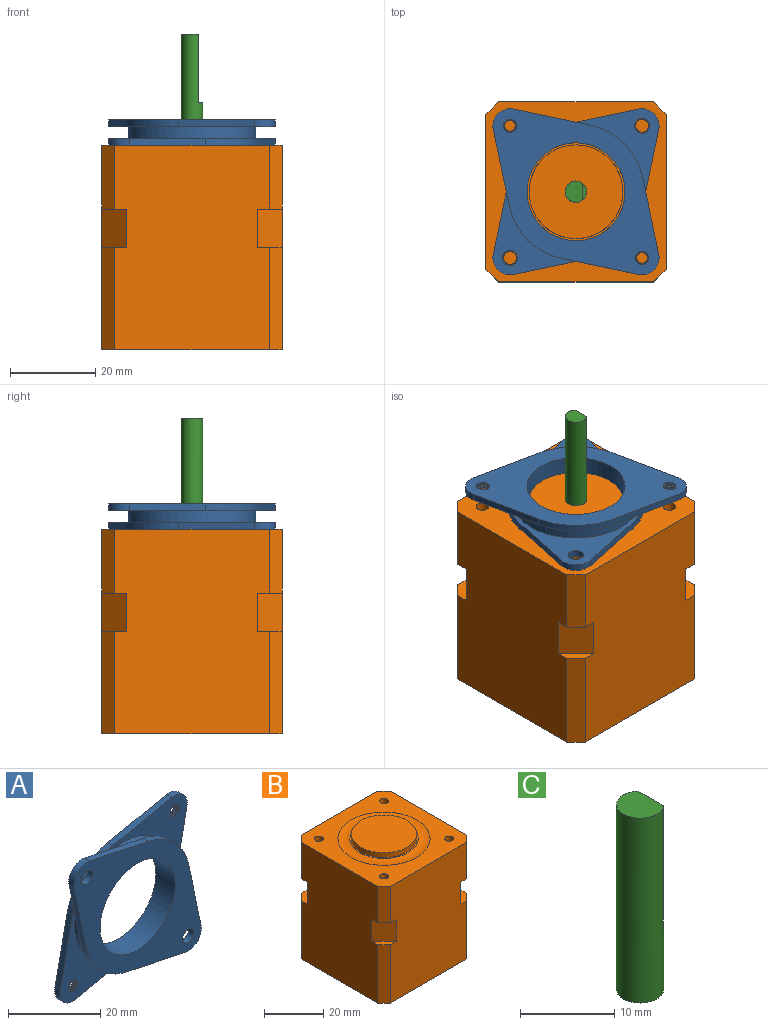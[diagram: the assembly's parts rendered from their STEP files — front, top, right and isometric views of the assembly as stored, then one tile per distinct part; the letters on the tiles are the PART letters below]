
ASSEMBLY  parts=3 mates=2
PART A: 32 faces, bbox 39.1x6.2x39.1 mm
  f0: cylinder r=1.75mm len=3.5mm, axis (0,1,0), area 17.6mm2, adj f10,f11
  f1: cylinder r=1.75mm len=3.5mm, axis (0,1,0), area 17.6mm2, adj f10,f11
  f2: plane 17.96x3.75mm, normal (-0.2,0,-0.98), area 29.3mm2, adj f3,f9,f10,f11
  f3: cylinder r=4mm len=4.82mm, axis (0,1,0), area 12.7mm2, adj f2,f4,f10,f11
  f4: plane 17.96x3.75mm, normal (0.98,0,0.2), area 29.3mm2, adj f3,f5,f10,f11
  f5: cylinder r=16mm len=12.39mm, axis (0,1,0), area 29.7mm2, adj f4,f6,f10,f11
  f6: plane 17.96x3.75mm, normal (0.2,0,0.98), area 29.3mm2, adj f5,f7,f10,f11
  f7: cylinder r=4mm len=4.82mm, axis (0,1,0), area 12.7mm2, adj f6,f8,f10,f11
  f8: plane 17.96x3.75mm, normal (-0.98,0,-0.2), area 29.3mm2, adj f7,f9,f10,f11
  f9: cylinder r=16mm len=12.39mm, axis (0,1,0), area 29.7mm2, adj f2,f8,f10,f11
  f10: plane 39x39mm, normal (0,1,0), area 336mm2, adj f0,f1,f2,f3,f4,f5,f6,f7
  f11: plane 39x39mm, normal (0,-1,0), area 627.4mm2, adj f0,f1,f2,f3,f4,f5,f6,f7
  f12: plane 39.14x39.14mm, normal (0,1,0), area 633.9mm2, adj f14,f15,f16,f17,f18,f19,f20,f21
  f13: cylinder r=15mm len=30mm, axis (0,1,0), area 254.5mm2, adj f10,f31
  f14: cylinder r=11.5mm len=23mm, axis (0,-1,0), area 426.3mm2, adj f11,f12
  f15: cylinder r=1.54mm len=3.09mm, axis (0,1,0), area 3.6mm2, adj f12,f16,f17,f31
  f16: bspline ~3.58x3.57mm, area 9.1mm2, adj f12,f15,f22,f31
  f17: bspline ~3.59x3.58mm, area 9.1mm2, adj f12,f15,f22,f31
  f18: cylinder r=1.54mm len=3.09mm, axis (0,1,0), area 3.6mm2, adj f12,f19,f20,f31
  f19: bspline ~3.58x3.57mm, area 9.1mm2, adj f12,f18,f21,f31
  f20: bspline ~3.59x3.58mm, area 9.1mm2, adj f12,f18,f21,f31
  f21: cylinder r=1.26mm len=2.53mm, axis (0,1,0), area 1.5mm2, adj f12,f19,f20,f31
  f22: cylinder r=1.26mm len=2.53mm, axis (0,1,0), area 1.5mm2, adj f12,f16,f17,f31
  f23: plane 17.96x3.75mm, normal (0.2,0,-0.98), area 29.3mm2, adj f12,f24,f30,f31
  f24: cylinder r=16mm len=12.39mm, axis (0,1,0), area 29.7mm2, adj f12,f23,f25,f31
  f25: plane 17.96x3.75mm, normal (0.98,0,-0.2), area 29.3mm2, adj f12,f24,f26,f31
  f26: cylinder r=4mm len=4.82mm, axis (0,1,0), area 12.7mm2, adj f12,f25,f27,f31
  f27: plane 17.96x3.75mm, normal (-0.2,0,0.98), area 29.3mm2, adj f12,f26,f28,f31
  f28: cylinder r=16mm len=12.39mm, axis (0,1,0), area 29.7mm2, adj f12,f27,f29,f31
  f29: plane 17.96x3.75mm, normal (-0.98,0,0.2), area 29.3mm2, adj f12,f28,f30,f31
  f30: cylinder r=4mm len=4.82mm, axis (0,1,0), area 12.7mm2, adj f12,f23,f29,f31
  f31: plane 39.14x39.14mm, normal (0,-1,0), area 342.6mm2, adj f13,f15,f16,f17,f18,f19,f20,f21
PART B: 58 faces, bbox 42.3x42.3x50.1 mm
  f0: plane 5.83x5.83mm, normal (0,0,1), area 12.5mm2, adj f3,f4,f5,f12
  f1: plane 5.83x5.83mm, normal (0,0,1), area 12.5mm2, adj f3,f9,f10,f13
  f2: plane 5.83x5.83mm, normal (0,0,1), area 12.5mm2, adj f7,f8,f9,f14
  f3: plane 48x36.3mm, normal (0,1,0), area 1691.5mm2, adj f0,f1,f4,f10,f12,f13,f16,f18
  f4: plane 24x3mm, normal (-0.71,0.71,0), area 101.8mm2, adj f0,f3,f5,f37
  f5: plane 48x36.3mm, normal (-1,0,0), area 1691.5mm2, adj f0,f4,f6,f11,f12,f15,f16,f19
  f6: plane 24x3mm, normal (-0.71,-0.71,0), area 101.8mm2, adj f5,f7,f11,f37
  f7: plane 48x36.3mm, normal (0,-1,0), area 1691.5mm2, adj f2,f6,f8,f11,f14,f15,f16,f17
  f8: plane 24x3mm, normal (0.71,-0.71,0), area 101.8mm2, adj f2,f7,f9,f37
  f9: plane 48x36.3mm, normal (1,0,0), area 1691.5mm2, adj f1,f2,f8,f10,f13,f14,f16,f17
  f10: plane 24x3mm, normal (0.71,0.71,0), area 101.8mm2, adj f1,f3,f9,f37
  f11: plane 5.83x5.83mm, normal (0,0,1), area 12.5mm2, adj f5,f6,f7,f15
  f12: plane 9x5.83mm, normal (-0.71,0.71,0), area 74.2mm2, adj f0,f3,f5,f19
  f13: plane 9x5.83mm, normal (0.71,0.71,0), area 74.2mm2, adj f1,f3,f9,f18
  f14: plane 9x5.83mm, normal (0.71,-0.71,0), area 74.2mm2, adj f2,f7,f9,f17
  f15: plane 9x5.83mm, normal (-0.71,-0.71,0), area 74.2mm2, adj f5,f7,f11,f24
  f16: plane 42.3x42.3mm, normal (0,0,1), area 988.2mm2, adj f3,f5,f7,f9,f20,f21,f22,f23
  f17: plane 5.83x5.83mm, normal (0,0,-1), area 12.5mm2, adj f7,f9,f14,f22
  f18: plane 5.83x5.83mm, normal (0,0,-1), area 12.5mm2, adj f3,f9,f13,f21
  f19: plane 5.83x5.83mm, normal (0,0,-1), area 12.5mm2, adj f3,f5,f12,f20
  f20: plane 15x3mm, normal (-0.71,0.71,0), area 63.6mm2, adj f3,f5,f16,f19
  f21: plane 15x3mm, normal (0.71,0.71,0), area 63.6mm2, adj f3,f9,f16,f18
  f22: plane 15x3mm, normal (0.71,-0.71,0), area 63.6mm2, adj f7,f9,f16,f17
  f23: plane 15x3mm, normal (-0.71,-0.71,0), area 63.6mm2, adj f5,f7,f16,f24
  f24: plane 5.83x5.83mm, normal (0,0,-1), area 12.5mm2, adj f5,f7,f15,f23
  f25: cylinder r=1.5mm len=5.5mm, axis (0,0,1), area 51.8mm2, adj f16,f26
  f26: plane 3x3mm, normal (0,0,1), area 7.1mm2, adj f25
  f27: cylinder r=1.5mm len=5.5mm, axis (0,0,1), area 51.8mm2, adj f16,f28
  f28: plane 3x3mm, normal (0,0,1), area 7.1mm2, adj f27
  f29: cylinder r=1.5mm len=5.5mm, axis (0,0,1), area 51.8mm2, adj f16,f30
  f30: plane 3x3mm, normal (0,0,1), area 7.1mm2, adj f29
  f31: cylinder r=1.5mm len=5.5mm, axis (0,0,1), area 51.8mm2, adj f16,f32
  f32: plane 3x3mm, normal (0,0,1), area 7.1mm2, adj f31
  f33: torus R=13.5mm, axis (0,0,-1), area 342.9mm2, adj f16,f34
  f34: plane 23x23mm, normal (0,0,1), area 35.3mm2, adj f33,f35
  f35: cylinder r=11mm len=22mm, axis (0,0,-1), area 138.2mm2, adj f34,f36
  f36: plane 22x22mm, normal (0,0,1), area 380.1mm2, adj f35
  f37: plane 42.3x42.3mm, normal (0,0,-1), area 1626mm2, adj f3,f4,f5,f6,f7,f8,f9,f10
  f38: plane 5x5mm, normal (0,0,-1), area 19.6mm2, adj f39
  f39: cylinder r=2.5mm len=5mm, axis (0,0,1), area 15.7mm2, adj f38,f40
  f40: plane 8x8mm, normal (0,0,-1), area 30.6mm2, adj f39,f41
  f41: cylinder r=4mm len=11mm, axis (0,0,-1), area 276.5mm2, adj f37,f40
  f42: plane 3x3mm, normal (0,0,-1), area 7.1mm2, adj f43
  f43: cylinder r=1.5mm len=4.5mm, axis (0,0,-1), area 42.4mm2, adj f42,f44
  f44: plane 5.5x5.5mm, normal (0,0,-1), area 16.7mm2, adj f43,f45
  f45: cylinder r=2.75mm len=10mm, axis (0,0,-1), area 172.8mm2, adj f37,f44
  f46: plane 3x3mm, normal (0,0,-1), area 7.1mm2, adj f47
  f47: cylinder r=1.5mm len=4.5mm, axis (0,0,-1), area 42.4mm2, adj f46,f48
  f48: plane 5.5x5.5mm, normal (0,0,-1), area 16.7mm2, adj f47,f49
  f49: cylinder r=2.75mm len=10mm, axis (0,0,-1), area 172.8mm2, adj f37,f48
  f50: plane 3x3mm, normal (0,0,-1), area 7.1mm2, adj f51
  f51: cylinder r=1.5mm len=4.5mm, axis (0,0,-1), area 42.4mm2, adj f50,f52
  f52: plane 5.5x5.5mm, normal (0,0,-1), area 16.7mm2, adj f51,f53
  f53: cylinder r=2.75mm len=10mm, axis (0,0,-1), area 172.8mm2, adj f37,f52
  f54: plane 3x3mm, normal (0,0,-1), area 7.1mm2, adj f55
  f55: cylinder r=1.5mm len=4.5mm, axis (0,0,-1), area 42.4mm2, adj f54,f56
  f56: plane 5.5x5.5mm, normal (0,0,-1), area 16.7mm2, adj f55,f57
  f57: cylinder r=2.75mm len=10mm, axis (0,0,-1), area 172.8mm2, adj f37,f56
PART C: 5 faces, bbox 5x5x24 mm
  f0: cylinder r=2.5mm len=24mm, axis (0,0,-1), area 306.9mm2, adj f1,f2,f3,f4
  f1: plane 5x4.1mm, normal (0,0,1), area 17.2mm2, adj f0,f3
  f2: plane 5x5mm, normal (0,0,-1), area 19.6mm2, adj f0
  f3: plane 16x3.84mm, normal (1,0,0), area 61.5mm2, adj f0,f1,f4
  f4: plane 3.84x0.9mm, normal (0,0,1), area 2.4mm2, adj f0,f3
PLACE A rot(axis=(1,0,0),90deg) t=(-16.56,-8.46,-12.35)mm
PLACE B t=(-16.56,-58.46,-51.35)mm
PLACE C t=(-16.56,-8.46,-51.35)mm
MATE fastened A.f1 <-> B.f31  axis (0,0,-1) through (-32.06,-23.96,-12.35)mm
MATE revolute B.f35 <-> C.f0  axis (0,0,1) through (-16.56,-8.46,-10.35)mm
